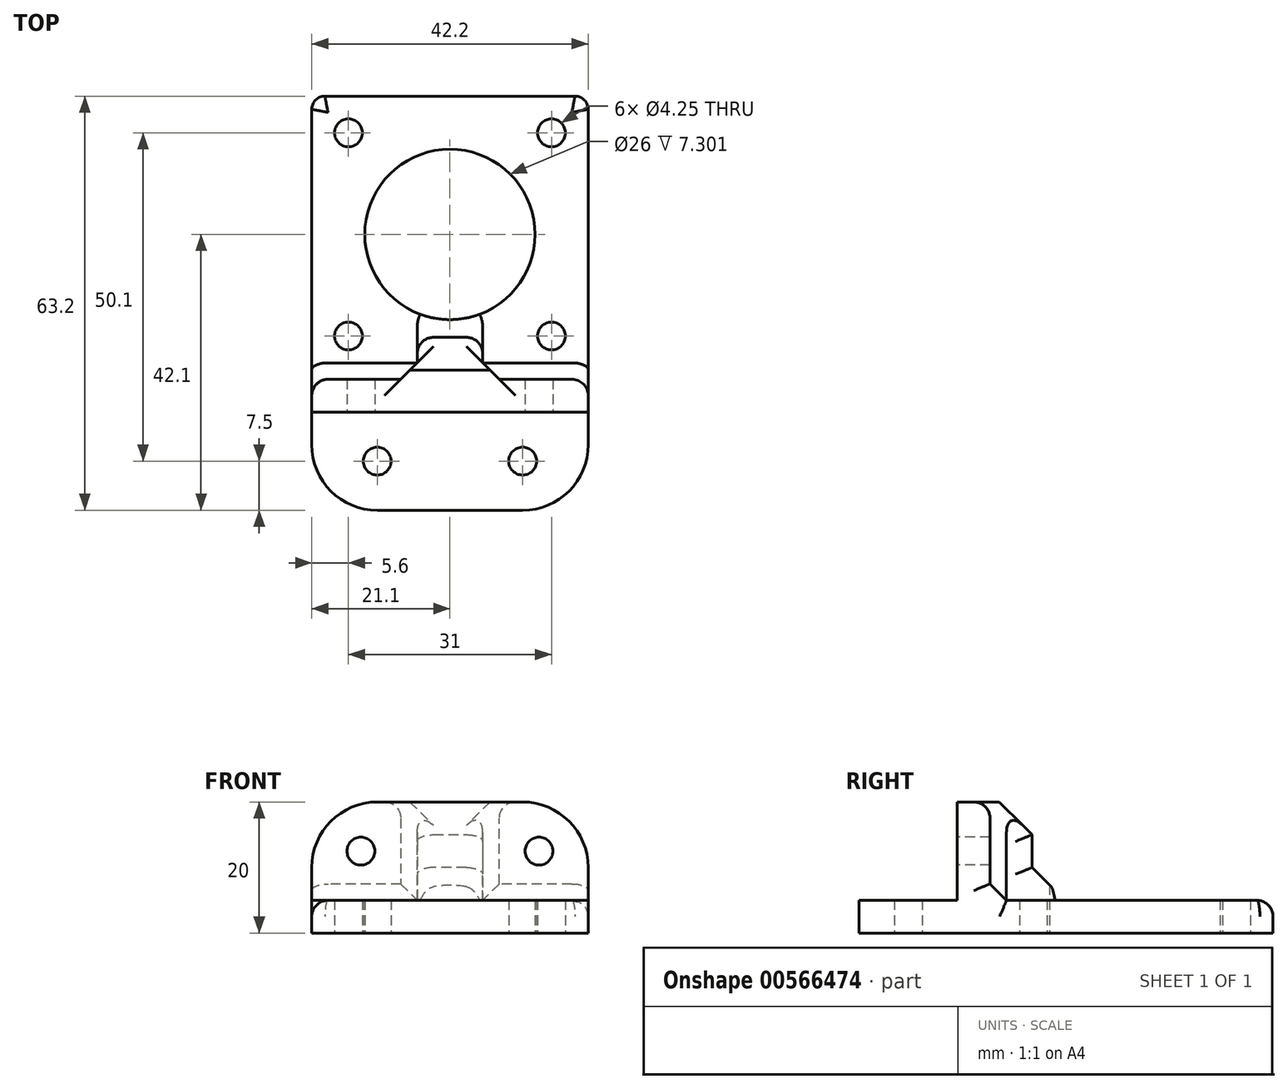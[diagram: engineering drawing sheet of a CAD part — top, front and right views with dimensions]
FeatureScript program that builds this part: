
annotation { "Feature Type Name" : "Feature", "Feature Type Description" : "" }
export const myFeature = defineFeature(function(context is Context, id is Id, definition is map)
    precondition{}
    {
        {
            var Q0;
            Q0=qCreatedBy(makeId("Top.planeOp"),FACE);
            var sketch = newSketch(context, id + "F0", { "sketchPlane" : qUnion([Q0])});
            skCircle(sketch, "E0", {"center": v(0, 0) * mm, "radius": 13 * mm});
            skLineSegment(sketch, "E1.bottom", {"start": v(15.5, -15.5) * mm, "end": v(-15.5, -15.5) * mm, "construction": true});
            skLineSegment(sketch, "E1.top", {"start": v(15.5, 15.5) * mm, "end": v(-15.5, 15.5) * mm, "construction": true});
            skLineSegment(sketch, "E1.left", {"start": v(15.5, -15.5) * mm, "end": v(15.5, 15.5) * mm, "construction": true});
            skLineSegment(sketch, "E1.right", {"start": v(-15.5, -15.5) * mm, "end": v(-15.5, 15.5) * mm, "construction": true});
            skLineSegment(sketch, "E2.bottom", {"start": v(21.1, -21.1) * mm, "end": v(-21.1, -21.1) * mm, "construction": true});
            skLineSegment(sketch, "E2.top", {"start": v(21.1, 21.1) * mm, "end": v(-21.1, 21.1) * mm});
            skLineSegment(sketch, "E2.left", {"start": v(21.1, -21.1) * mm, "end": v(21.1, 21.1) * mm});
            skLineSegment(sketch, "E2.right", {"start": v(-21.1, -21.1) * mm, "end": v(-21.1, 21.1) * mm});
            skCircle(sketch, "E3", {"center": v(-15.5, 15.5) * mm, "radius": 2.12 * mm});
            skCircle(sketch, "E4", {"center": v(15.5, 15.5) * mm, "radius": 2.12 * mm});
            skCircle(sketch, "E5", {"center": v(15.5, -15.5) * mm, "radius": 2.12 * mm});
            skCircle(sketch, "E6", {"center": v(-15.5, -15.5) * mm, "radius": 2.12 * mm});
            skLineSegment(sketch, "E7", {"start": v(-21.1, -21.1) * mm, "end": v(-21.1, -22.1) * mm});
            skLineSegment(sketch, "E8", {"start": v(-21.1, -22.1) * mm, "end": v(-21.1, -42.1) * mm});
            skLineSegment(sketch, "E9", {"start": v(-21.1, -42.1) * mm, "end": v(0, -42.1) * mm});
            skLineSegment(sketch, "E10.MirrorCS", {"start": v(21.1, -42.1) * mm, "end": v(0, -42.1) * mm});
            skLineSegment(sketch, "E11.MirrorCS", {"start": v(21.1, -22.1) * mm, "end": v(21.1, -42.1) * mm});
            skLineSegment(sketch, "E12.MirrorCS", {"start": v(21.1, -21.1) * mm, "end": v(21.1, -22.1) * mm});
            skCircle(sketch, "E13", {"center": v(-11.1, -34.6) * mm, "radius": 2.12 * mm});
            skCircle(sketch, "E14.MirrorC", {"center": v(11.1, -34.6) * mm, "radius": 2.12 * mm});
            skSolve(sketch);
        }
        {
            var Q0;
            Q0=qSketchRegion(id+"F0",true);
            extrude(context, id + "F1", {"entities" : qUnion([Q0]), "depth" : 5 * mm});
        }
        {
            var Q0;
            Q0=makeQuery(id+"F1.opExtrude","CAP_FACE",FACE,{"disambiguationData":[OSD([sQuery(id+"F0.wireOp",EDGE,"E0"),sQuery(id+"F0.wireOp",EDGE,"E2.top"),sQuery(id+"F0.wireOp",EDGE,"E2.left"),sQuery(id+"F0.wireOp",EDGE,"E2.right"),sQuery(id+"F0.wireOp",EDGE,"E3"),sQuery(id+"F0.wireOp",EDGE,"E4"),sQuery(id+"F0.wireOp",EDGE,"E5"),sQuery(id+"F0.wireOp",EDGE,"E6"),sQuery(id+"F0.wireOp",EDGE,"E7"),sQuery(id+"F0.wireOp",EDGE,"1TxZPYh5-fuEI-jFA4-MOYT-LekiY9hf7Zo8"),sQuery(id+"F0.wireOp",EDGE,"E8"),sQuery(id+"F0.wireOp",EDGE,"E9"),sQuery(id+"F0.wireOp",EDGE,"E10.MirrorCS"),sQuery(id+"F0.wireOp",EDGE,"E11.MirrorCS"),sQuery(id+"F0.wireOp",EDGE,"6e6b97e5-768a-42da-bacb-a23eddf443a30.MirrorCS"),sQuery(id+"F0.wireOp",EDGE,"E12.MirrorCS"),sQuery(id+"F0.wireOp",EDGE,"E13"),sQuery(id+"F0.wireOp",EDGE,"E14.MirrorC")])],"isStart":false});
            var sketch = newSketch(context, id + "F2", { "sketchPlane" : qUnion([Q0])});
            skLineSegment(sketch, "E15.bottom", {"start": v(-21.1, -22.1) * mm, "end": v(-5, -22.1) * mm});
            skLineSegment(sketch, "E15.top", {"start": v(-21.1, -27.1) * mm, "end": v(21.1, -27.1) * mm});
            skLineSegment(sketch, "E15.left", {"start": v(-21.1, -22.1) * mm, "end": v(-21.1, -27.1) * mm});
            skLineSegment(sketch, "E15.right", {"start": v(21.1, -22.1) * mm, "end": v(21.1, -27.1) * mm});
            skLineSegment(sketch, "E16", {"start": v(-5, -22.1) * mm, "end": v(-5, -15.7) * mm});
            skLineSegment(sketch, "E17", {"start": v(-5, -15.7) * mm, "end": v(0, -15.7) * mm});
            skLineSegment(sketch, "E18.MirrorCS", {"start": v(5, -15.7) * mm, "end": v(0, -15.7) * mm});
            skLineSegment(sketch, "E19.MirrorCS", {"start": v(5, -22.1) * mm, "end": v(5, -15.7) * mm});
            skLineSegment(sketch, "E20.trimOffspring", {"start": v(5, -22.1) * mm, "end": v(21.1, -22.1) * mm});
            skSolve(sketch);
        }
        {
            var Q0;
            Q0=qSketchRegion(id+"F2",true);
            extrude(context, id + "F3", {"entities" : qUnion([Q0]), "operationType" : NewBodyOperationType.ADD, "depth" : 15 * mm});
        }
        {
            var Q0;
            Q0=makeQuery(id+"F3.opExtrude","SWEPT_FACE",FACE,{"disambiguationData":[OSD([sQuery(id+"F2.wireOp",EDGE,"E15.top")])]});
            var sketch = newSketch(context, id + "F4", { "sketchPlane" : qUnion([Q0])});
            skCircle(sketch, "E21", {"center": v(-13.6, 12.5) * mm, "radius": 2.12 * mm});
            skCircle(sketch, "E22.MirrorC", {"center": v(13.6, 12.5) * mm, "radius": 2.12 * mm});
            skSolve(sketch);
        }
        {
            var Q0;
            Q0=qSketchRegion(id+"F4",true);
            extrude(context, id + "F5", {"entities" : qUnion([Q0]), "operationType" : NewBodyOperationType.REMOVE, "oppositeDirection" : true, "depth" : 25 * mm});
        }
        {
            var Q0;
            Q0=makeQuery(id+"F1.opExtrude","SWEPT_EDGE",EDGE,{"disambiguationData":[OSD([sQuery(id+"F0.wireOp",EDGE,"E8"),sQuery(id+"F0.wireOp",EDGE,"E9")])]});
            var Q1;
            Q1=makeQuery(id+"F1.opExtrude","SWEPT_EDGE",EDGE,{"disambiguationData":[OSD([sQuery(id+"F0.wireOp",EDGE,"E10.MirrorCS"),sQuery(id+"F0.wireOp",EDGE,"E11.MirrorCS")])]});
            var Q2;
            Q2=makeQuery(id+"F3.opExtrude","CAP_EDGE",EDGE,{"disambiguationData":[OSD([sQuery(id+"F2.wireOp",EDGE,"Z7c0iSkX-skyO-crxs-Fnz0-ssCoRv2q4eRB.left")])],"isStart":false});
            var Q3;
            Q3=makeQuery(id+"F3.opExtrude","CAP_EDGE",EDGE,{"disambiguationData":[OSD([sQuery(id+"F2.wireOp",EDGE,"Z7c0iSkX-skyO-crxs-Fnz0-ssCoRv2q4eRB.right")])],"isStart":false});
            var Q4;
            Q4=makeQuery(id+"F3.opExtrude","CAP_EDGE",EDGE,{"disambiguationData":[OSD([sQuery(id+"F2.wireOp",EDGE,"E15.left")])],"isStart":false});
            var Q5;
            Q5=makeQuery(id+"F3.opExtrude","CAP_EDGE",EDGE,{"disambiguationData":[OSD([sQuery(id+"F2.wireOp",EDGE,"E15.right")])],"isStart":false});
            fillet(context, id + "F6", {"entities" : qUnion([Q0, Q1, Q2, Q3, Q4, Q5]), "radius" : 10 * mm, "tangentPropagation" : true, "allowEdgeOverflow" : false});
        }
        {
            var Q0;
            Q0=makeQuery(id+"F1.opExtrude","SWEPT_EDGE",EDGE,{"disambiguationData":[OSD([sQuery(id+"F0.wireOp",EDGE,"E2.top"),sQuery(id+"F0.wireOp",EDGE,"E2.right")])]});
            var Q1;
            Q1=makeQuery(id+"F1.opExtrude","SWEPT_EDGE",EDGE,{"disambiguationData":[OSD([sQuery(id+"F0.wireOp",EDGE,"E2.top"),sQuery(id+"F0.wireOp",EDGE,"E2.left")])]});
            fillet(context, id + "F7", {"entities" : qUnion([Q0, Q1]), "radius" : 2 * mm, "tangentPropagation" : true, "allowEdgeOverflow" : false});
        }
        {
            var Q0;
            Q0=makeQuery(id+"F3.opExtrude","CAP_EDGE",EDGE,{"disambiguationData":[OSD([sQuery(id+"F2.wireOp",EDGE,"E17"),sQuery(id+"F2.wireOp",EDGE,"E18.MirrorCS")])],"isStart":true});
            var Q1;
            Q1=makeQuery(id+"F3.opExtrude","CAP_EDGE",EDGE,{"disambiguationData":[OSD([sQuery(id+"F2.wireOp",EDGE,"E17"),sQuery(id+"F2.wireOp",EDGE,"E18.MirrorCS")])],"isStart":false});
            chamfer(context, id + "F8", {"entities" : qUnion([Q0, Q1]), "width" : 5 * mm, "tangentPropagation" : true});
        }
        {
            var Q0;
            Q0=makeQuery(id+"F3.opExtrude","CAP_EDGE",EDGE,{"disambiguationData":[OSD([sQuery(id+"F2.wireOp",EDGE,"E20.trimOffspring")])],"isStart":true});
            var Q1;
            Q1=makeQuery(id+"F3.opExtrude","CAP_EDGE",EDGE,{"disambiguationData":[OSD([sQuery(id+"F2.wireOp",EDGE,"E15.bottom")])],"isStart":true});
            var Q2;
            Q2=makeQuery(id+"F3.opExtrude","SWEPT_EDGE",EDGE,{"disambiguationData":[OSD([sQuery(id+"F2.wireOp",EDGE,"E15.bottom"),sQuery(id+"F2.wireOp",EDGE,"E16")])]});
            var Q3;
            Q3=makeQuery(id+"F3.opExtrude","SWEPT_EDGE",EDGE,{"disambiguationData":[OSD([sQuery(id+"F2.wireOp",EDGE,"E19.MirrorCS"),sQuery(id+"F2.wireOp",EDGE,"E20.trimOffspring")])]});
            chamfer(context, id + "F9", {"entities" : qUnion([Q0, Q1, Q2, Q3]), "width" : 2.5 * mm, "tangentPropagation" : true});
        }
        {
            var Q0;
            Q0=makeQuery(id+"F8.opChamfer","BLEND_EDGE",EDGE,{"blendedFrom":[makeQuery(id+"F3.opExtrude","CAP_EDGE",EDGE,{"disambiguationData":[OSD([sQuery(id+"F2.wireOp",EDGE,"E17"),sQuery(id+"F2.wireOp",EDGE,"E18.MirrorCS")])],"isStart":false}),makeQuery(id+"F3.opExtrude","SWEPT_FACE",FACE,{"disambiguationData":[OSD([sQuery(id+"F2.wireOp",EDGE,"E16")])]})],"blendedInto":[makeQuery(id+"F3.opExtrude","SWEPT_FACE",FACE,{"disambiguationData":[OSD([sQuery(id+"F2.wireOp",EDGE,"E16")])]})]});
            var Q1;
            Q1=makeQuery(id+"F8.opChamfer","BLEND_EDGE",EDGE,{"blendedFrom":[makeQuery(id+"F3.opExtrude","CAP_EDGE",EDGE,{"disambiguationData":[OSD([sQuery(id+"F2.wireOp",EDGE,"E17"),sQuery(id+"F2.wireOp",EDGE,"E18.MirrorCS")])],"isStart":true}),makeQuery(id+"F3.opExtrude","SWEPT_FACE",FACE,{"disambiguationData":[OSD([sQuery(id+"F2.wireOp",EDGE,"E16")])]})],"blendedInto":[makeQuery(id+"F3.opExtrude","SWEPT_FACE",FACE,{"disambiguationData":[OSD([sQuery(id+"F2.wireOp",EDGE,"E16")])]})]});
            var Q2;
            Q2=makeQuery(id+"F8.opChamfer","BLEND_EDGE",EDGE,{"blendedFrom":[makeQuery(id+"F3.opExtrude","CAP_EDGE",EDGE,{"disambiguationData":[OSD([sQuery(id+"F2.wireOp",EDGE,"E17"),sQuery(id+"F2.wireOp",EDGE,"E18.MirrorCS")])],"isStart":true}),makeQuery(id+"F3.opExtrude","SWEPT_FACE",FACE,{"disambiguationData":[OSD([sQuery(id+"F2.wireOp",EDGE,"E19.MirrorCS")])]})],"blendedInto":[makeQuery(id+"F3.opExtrude","SWEPT_FACE",FACE,{"disambiguationData":[OSD([sQuery(id+"F2.wireOp",EDGE,"E19.MirrorCS")])]})]});
            var Q3;
            Q3=makeQuery(id+"F8.opChamfer","BLEND_EDGE",EDGE,{"blendedFrom":[makeQuery(id+"F3.opExtrude","CAP_EDGE",EDGE,{"disambiguationData":[OSD([sQuery(id+"F2.wireOp",EDGE,"E17"),sQuery(id+"F2.wireOp",EDGE,"E18.MirrorCS")])],"isStart":false}),makeQuery(id+"F3.opExtrude","SWEPT_FACE",FACE,{"disambiguationData":[OSD([sQuery(id+"F2.wireOp",EDGE,"E19.MirrorCS")])]})],"blendedInto":[makeQuery(id+"F3.opExtrude","SWEPT_FACE",FACE,{"disambiguationData":[OSD([sQuery(id+"F2.wireOp",EDGE,"E19.MirrorCS")])]})]});
            var Q4;
            Q4=makeQuery(id+"F3.opExtrude","SWEPT_EDGE",EDGE,{"disambiguationData":[OSD([sQuery(id+"F2.wireOp",EDGE,"E18.MirrorCS"),sQuery(id+"F2.wireOp",EDGE,"E19.MirrorCS")])]});
            var Q5;
            Q5=makeQuery(id+"F3.opExtrude","SWEPT_EDGE",EDGE,{"disambiguationData":[OSD([sQuery(id+"F2.wireOp",EDGE,"E16"),sQuery(id+"F2.wireOp",EDGE,"E17")])]});
            var Q6;
            Q6=makeQuery(id+"F6.opFillet","BLEND_EDGE",EDGE,{"blendedFrom":[makeQuery(id+"F3.opExtrude","CAP_EDGE",EDGE,{"disambiguationData":[OSD([sQuery(id+"F2.wireOp",EDGE,"E15.left")])],"isStart":false}),makeQuery(id+"F3.opExtrude","SWEPT_FACE",FACE,{"disambiguationData":[OSD([sQuery(id+"F2.wireOp",EDGE,"E15.bottom")])]})],"blendedInto":[makeQuery(id+"F3.opExtrude","SWEPT_FACE",FACE,{"disambiguationData":[OSD([sQuery(id+"F2.wireOp",EDGE,"E15.bottom")])]})]});
            var Q7;
            Q7=makeQuery(id+"F6.opFillet","BLEND_EDGE",EDGE,{"blendedFrom":[makeQuery(id+"F3.opExtrude","CAP_EDGE",EDGE,{"disambiguationData":[OSD([sQuery(id+"F2.wireOp",EDGE,"E15.right")])],"isStart":false}),makeQuery(id+"F3.opExtrude","SWEPT_FACE",FACE,{"disambiguationData":[OSD([sQuery(id+"F2.wireOp",EDGE,"E20.trimOffspring")])]})],"blendedInto":[makeQuery(id+"F3.opExtrude","SWEPT_FACE",FACE,{"disambiguationData":[OSD([sQuery(id+"F2.wireOp",EDGE,"E20.trimOffspring")])]})]});
            var Q8;
            {var subQ0=sQuery(id+"F0.wireOp",EDGE,"E8");var subQ1=sQuery(id+"F0.wireOp",EDGE,"E7");var subQ2=sQuery(id+"F0.wireOp",EDGE,"E2.right");var subQ3=sQuery(id+"F0.wireOp",EDGE,"E2.top");Q8=makeQuery(id+"F3.boolean.opBoolean","SPLIT",EDGE,{"disambiguationData":[TD([makeQuery(id+"F1.opExtrude","SWEPT_FACE",FACE,{"disambiguationData":[OSD([subQ3])]})])],"derivedFrom":makeQuery(id+"F1.opExtrude","CAP_EDGE",EDGE,{"disambiguationData":[OSD([subQ2,subQ1,subQ0])],"isStart":false})});}
            var Q9;
            Q9=makeQuery(id+"F9.opChamfer","BLEND_EDGE",EDGE,{"blendedFrom":[makeQuery(id+"F3.opExtrude","CAP_EDGE",EDGE,{"disambiguationData":[OSD([sQuery(id+"F2.wireOp",EDGE,"E15.bottom")])],"isStart":true}),makeQuery(id+"F3.boolean.opBoolean","MERGE",FACE,{"derivedFrom":[makeQuery(id+"F1.opExtrude","SWEPT_FACE",FACE,{"disambiguationData":[OSD([sQuery(id+"F0.wireOp",EDGE,"E2.right"),sQuery(id+"F0.wireOp",EDGE,"E7"),sQuery(id+"F0.wireOp",EDGE,"E8")])]}),makeQuery(id+"F3.opExtrude","SWEPT_FACE",FACE,{"disambiguationData":[OSD([sQuery(id+"F2.wireOp",EDGE,"E15.left")])]})]})],"blendedInto":[makeQuery(id+"F3.boolean.opBoolean","MERGE",FACE,{"derivedFrom":[makeQuery(id+"F1.opExtrude","SWEPT_FACE",FACE,{"disambiguationData":[OSD([sQuery(id+"F0.wireOp",EDGE,"E2.right"),sQuery(id+"F0.wireOp",EDGE,"E7"),sQuery(id+"F0.wireOp",EDGE,"E8")])]}),makeQuery(id+"F3.opExtrude","SWEPT_FACE",FACE,{"disambiguationData":[OSD([sQuery(id+"F2.wireOp",EDGE,"E15.left")])]})]})]});
            var Q10;
            Q10=makeQuery(id+"F9.opChamfer","BLEND_EDGE",EDGE,{"blendedFrom":[makeQuery(id+"F3.opExtrude","CAP_EDGE",EDGE,{"disambiguationData":[OSD([sQuery(id+"F2.wireOp",EDGE,"E20.trimOffspring")])],"isStart":true}),makeQuery(id+"F3.boolean.opBoolean","MERGE",FACE,{"derivedFrom":[makeQuery(id+"F1.opExtrude","SWEPT_FACE",FACE,{"disambiguationData":[OSD([sQuery(id+"F0.wireOp",EDGE,"E2.left"),sQuery(id+"F0.wireOp",EDGE,"E11.MirrorCS"),sQuery(id+"F0.wireOp",EDGE,"E12.MirrorCS")])]}),makeQuery(id+"F3.opExtrude","SWEPT_FACE",FACE,{"disambiguationData":[OSD([sQuery(id+"F2.wireOp",EDGE,"E15.right")])]})]})],"blendedInto":[makeQuery(id+"F3.boolean.opBoolean","MERGE",FACE,{"derivedFrom":[makeQuery(id+"F1.opExtrude","SWEPT_FACE",FACE,{"disambiguationData":[OSD([sQuery(id+"F0.wireOp",EDGE,"E2.left"),sQuery(id+"F0.wireOp",EDGE,"E11.MirrorCS"),sQuery(id+"F0.wireOp",EDGE,"E12.MirrorCS")])]}),makeQuery(id+"F3.opExtrude","SWEPT_FACE",FACE,{"disambiguationData":[OSD([sQuery(id+"F2.wireOp",EDGE,"E15.right")])]})]})]});
            fillet(context, id + "F10", {"entities" : qUnion([Q0, Q1, Q2, Q3, Q4, Q5, Q6, Q7, Q8, Q9, Q10]), "radius" : 2.5 * mm, "tangentPropagation" : true, "allowEdgeOverflow" : false});
        }
    });
